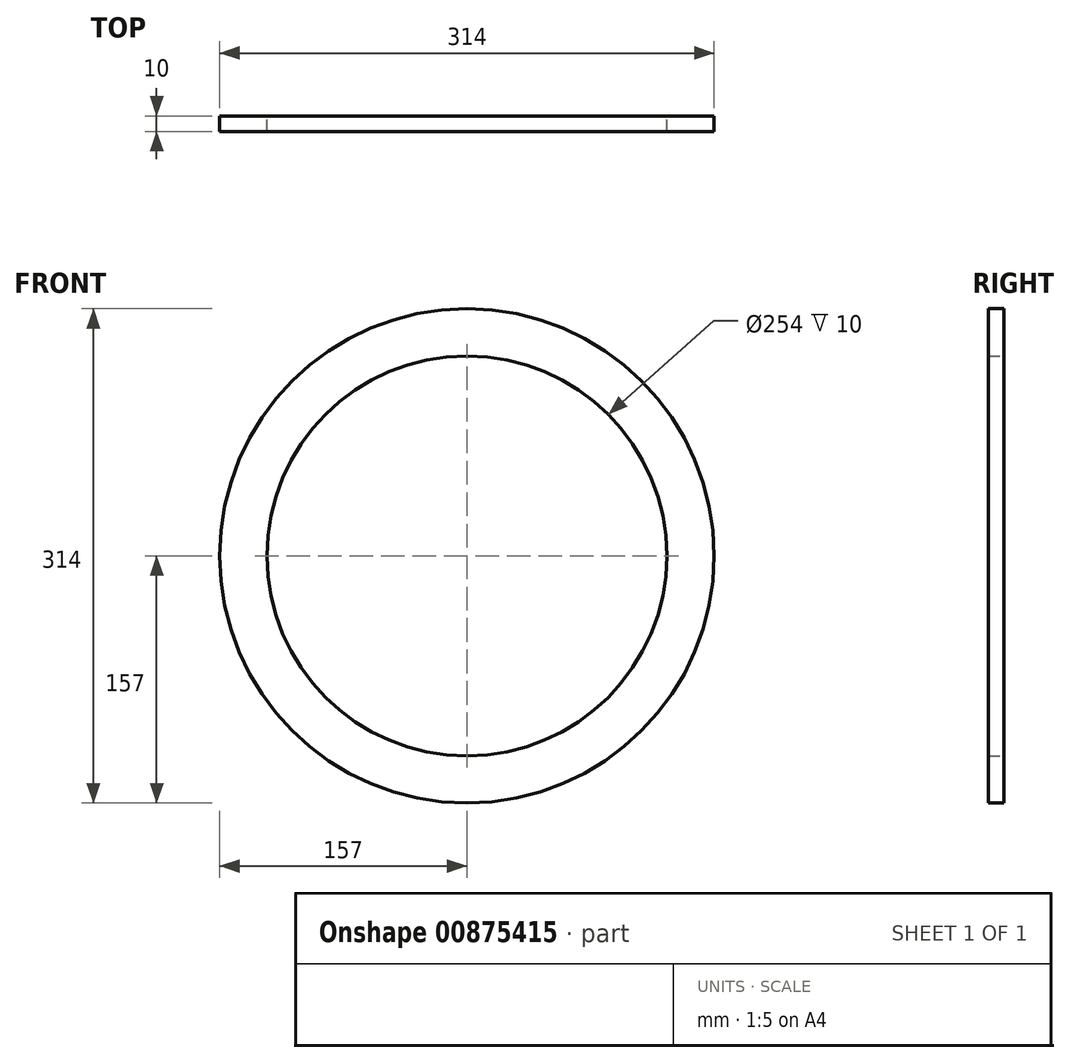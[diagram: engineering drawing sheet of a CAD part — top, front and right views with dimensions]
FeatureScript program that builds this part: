
annotation { "Feature Type Name" : "Feature", "Feature Type Description" : "" }
export const myFeature = defineFeature(function(context is Context, id is Id, definition is map)
    precondition{}
    {
        {
            var Q0;
            Q0=qCreatedBy(makeId("Right.planeOp"),FACE);
            var sketch = newSketch(context, id + "F0", { "sketchPlane" : qUnion([Q0])});
            skLineSegment(sketch, "E0.bottom", {"start": v(0, 157) * mm, "end": v(10, 157) * mm});
            skLineSegment(sketch, "E0.top", {"start": v(0, 127) * mm, "end": v(10, 127) * mm});
            skLineSegment(sketch, "E0.left", {"start": v(0, 157) * mm, "end": v(0, 127) * mm});
            skLineSegment(sketch, "E0.right", {"start": v(10, 157) * mm, "end": v(10, 127) * mm});
            skLineSegment(sketch, "E1", {"start": v(52.1, 0) * mm, "end": v(-196.7, 0) * mm, "construction": true});
            skArc(sketch, "E2", {"start": v(70, 30) * mm, "mid": v(48.79, 21.21) * mm, "end": v(40, 0) * mm});
            skArc(sketch, "E3", {"start": v(0, 122.5) * mm, "mid": v(-5.22, 115) * mm, "end": v(0, 107.5) * mm});
            skLineSegment(sketch, "E4", {"start": v(0, 127) * mm, "end": v(0, 122.5) * mm});
            skFitSpline(sketch, "E5", {"points": [v(0, 107.5) * mm, v(30, 65) * mm, v(70, 30) * mm], "startDerivative": vector(60.32, -112.83) * mm, "endDerivative": vector(107.42, -88.81) * mm});
            skSolve(sketch);
        }
        {
            var Q0;
            Q0=makeQuery(id+"F0.imprint","IMPRINT",FACE,{"disambiguationData":[TD([[makeQuery(id+"F0.imprint","IMPRINT",EDGE,{"derivedFrom":sQuery(id+"F0.wireOp",EDGE,"E0.bottom")}),-1.0]])]});
            var Q1;
            Q1=sQuery(id+"F0.wireOp",EDGE,"E1");
            revolve(context, id + "F1", {"surfaceOperationType" : NewSurfaceOperationType.NEW, "entities" : qUnion([Q0]), "axis" : qUnion([Q1]), "revolveType" : RevolveType.FULL});
        }
    });
